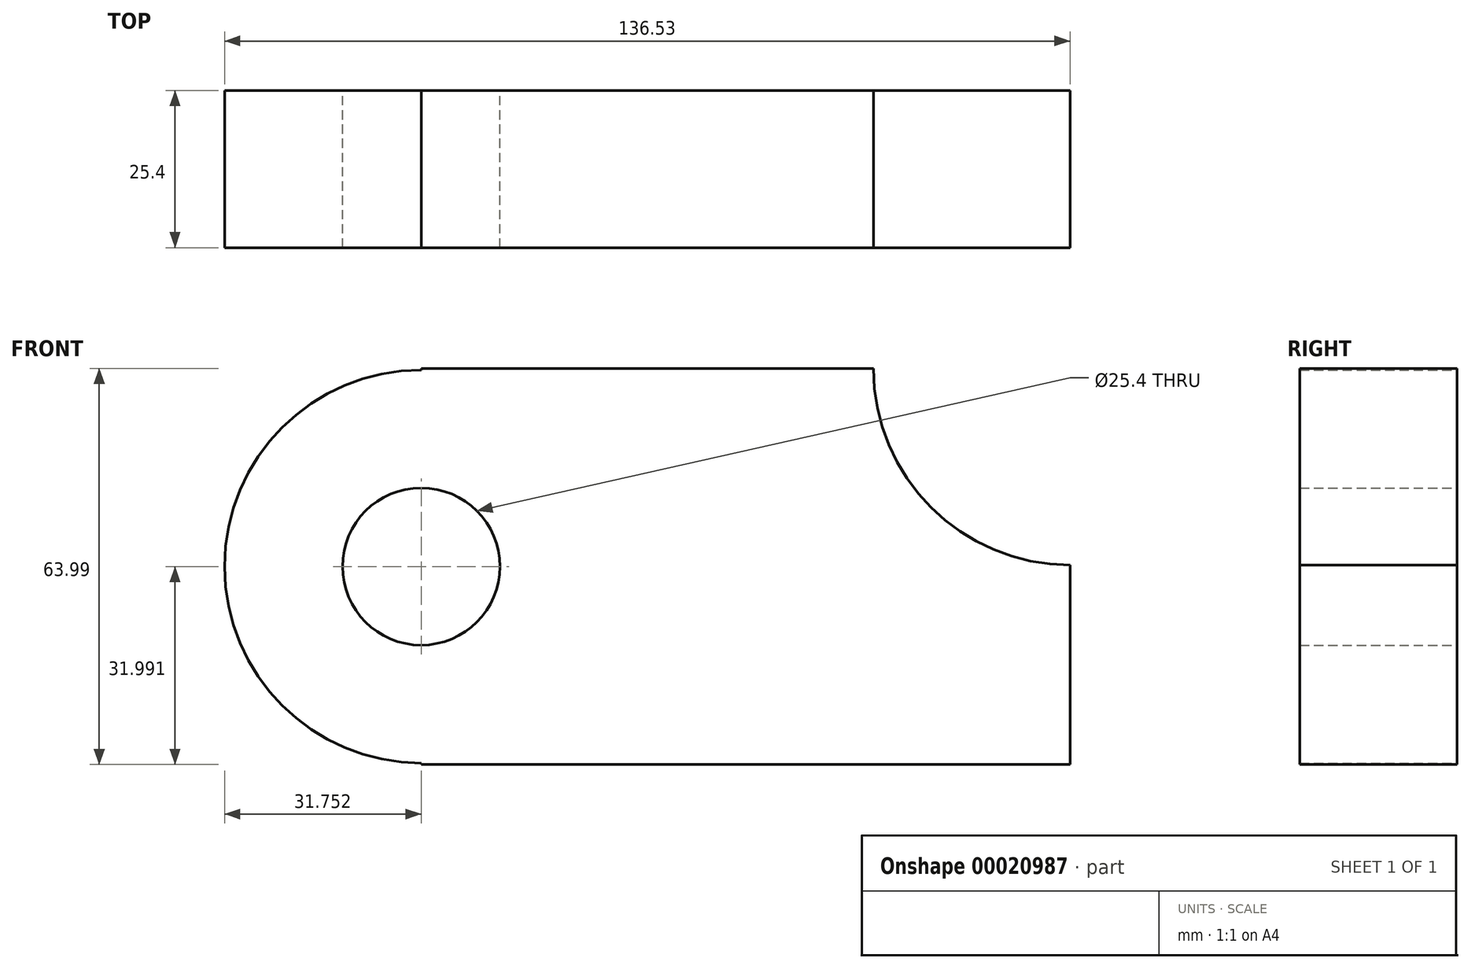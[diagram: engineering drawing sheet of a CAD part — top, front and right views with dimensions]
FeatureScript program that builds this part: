
annotation { "Feature Type Name" : "Feature", "Feature Type Description" : "" }
export const myFeature = defineFeature(function(context is Context, id is Id, definition is map)
    precondition{}
    {
        {
            var Q0;
            Q0=qCreatedBy(makeId("Front.planeOp"),FACE);
            var sketch = newSketch(context, id + "F0", { "sketchPlane" : qUnion([Q0])});
            skLineSegment(sketch, "E0.bottom", {"start": v(-23.58, 176.99) * mm, "end": v(49.45, 176.99) * mm});
            skLineSegment(sketch, "E0.top", {"start": v(-23.58, 113) * mm, "end": v(81.2, 113) * mm});
            skLineSegment(sketch, "E0.left", {"start": v(-23.58, 176.99) * mm, "end": v(-23.58, 157.7) * mm});
            skLineSegment(sketch, "E0.right", {"start": v(81.2, 145.24) * mm, "end": v(81.2, 113) * mm});
            skCircle(sketch, "E1", {"center": v(-23.58, 145) * mm, "radius": 31.75 * mm});
            skCircle(sketch, "E2", {"center": v(-23.58, 145) * mm, "radius": 12.7 * mm});
            skCircle(sketch, "E3", {"center": v(81.2, 176.99) * mm, "radius": 31.75 * mm});
            skLineSegment(sketch, "E4.trimOffspring", {"start": v(-23.58, 132.3) * mm, "end": v(-23.58, 113) * mm});
            skSolve(sketch);
        }
        {
            var Q0;
            {var subQ6=sQuery(id+"F0.wireOp",EDGE,"E0.bottom");Q0=makeQuery(id+"F0.imprint","IMPRINT",FACE,{"disambiguationData":[TD([[makeQuery(id+"F0.imprint","IMPRINT",EDGE,{"derivedFrom":subQ6}),-1.0]])]});}
            var Q1;
            {var subQ3=sQuery(id+"F0.wireOp",EDGE,"E2");var subQ5=sQuery(id+"F0.wireOp",EDGE,"E0.left");var subQ6=makeQuery(id+"F0.imprint","INTERSECT",VERTEX,{"derivedFrom":[subQ5,subQ3]});Q1=makeQuery(id+"F0.imprint","IMPRINT",FACE,{"disambiguationData":[TD([[makeQuery(id+"F0.imprint","IMPRINT",EDGE,{"disambiguationData":[TD([[subQ6,1.0]])],"derivedFrom":subQ5}),-1.0]])]});}
            var Q2;
            {var subQ3=sQuery(id+"F0.wireOp",EDGE,"E2");var subQ5=sQuery(id+"F0.wireOp",EDGE,"E0.left");var subQ6=makeQuery(id+"F0.imprint","INTERSECT",VERTEX,{"derivedFrom":[subQ5,subQ3]});Q2=makeQuery(id+"F0.imprint","IMPRINT",FACE,{"disambiguationData":[TD([[makeQuery(id+"F0.imprint","IMPRINT",EDGE,{"disambiguationData":[TD([[subQ6,1.0]])],"derivedFrom":subQ5}),1.0]])]});}
            extrude(context, id + "F1", {"entities" : qUnion([Q0, Q1, Q2]), "depth" : 25.4 * mm});
        }
    });
